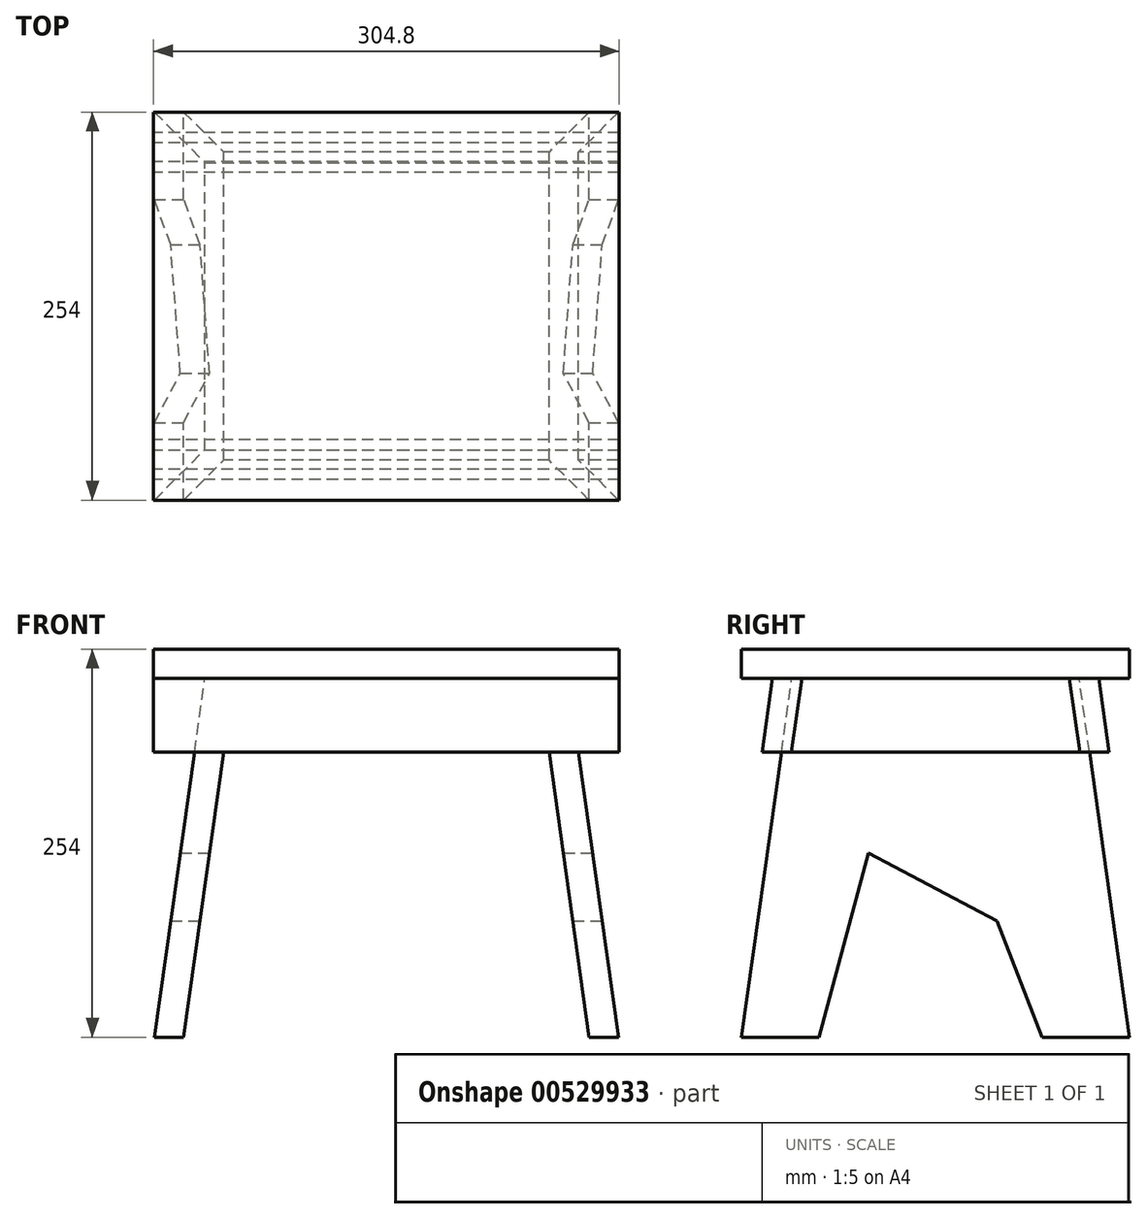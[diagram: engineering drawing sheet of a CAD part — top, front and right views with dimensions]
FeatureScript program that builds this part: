
annotation { "Feature Type Name" : "Feature", "Feature Type Description" : "" }
export const myFeature = defineFeature(function(context is Context, id is Id, definition is map)
    precondition{}
    {
        {
            var Q0;
            Q0=qCreatedBy(makeId("Front.planeOp"),FACE);
            var sketch = newSketch(context, id + "F0", { "sketchPlane" : qUnion([Q0])});
            skLineSegment(sketch, "E0.bottom", {"start": v(152.4, -9.53) * mm, "end": v(-152.4, -9.53) * mm, "construction": true});
            skLineSegment(sketch, "E0.top", {"start": v(152.4, 9.53) * mm, "end": v(-152.4, 9.52) * mm});
            skLineSegment(sketch, "E0.left", {"start": v(152.4, -9.53) * mm, "end": v(152.4, 9.52) * mm});
            skLineSegment(sketch, "E0.right", {"start": v(-152.4, -9.53) * mm, "end": v(-152.4, 9.52) * mm});
            skPoint(sketch, "E0.middle", {"position": v(0, 0) * mm});
            skLineSegment(sketch, "E1.bottom", {"start": v(-152.4, -9.53) * mm, "end": v(151.94, -9.52) * mm});
            skLineSegment(sketch, "E1.top", {"start": v(-152.4, -244.47) * mm, "end": v(151.94, -244.47) * mm, "construction": true});
            skLineSegment(sketch, "E1.left", {"start": v(-152.4, -9.53) * mm, "end": v(-152.4, -244.47) * mm, "construction": true});
            skLineSegment(sketch, "E1.right", {"start": v(151.94, -9.52) * mm, "end": v(151.94, -244.47) * mm, "construction": true});
            skLineSegment(sketch, "E2", {"start": v(118.92, -9.52) * mm, "end": v(151.94, -244.47) * mm});
            skLineSegment(sketch, "E3", {"start": v(99.68, -9.53) * mm, "end": v(132.7, -244.47) * mm});
            skLineSegment(sketch, "E4", {"start": v(99.68, -9.52) * mm, "end": v(118.92, -9.52) * mm});
            skLineSegment(sketch, "E5.MirrorCS", {"start": v(-99.68, -9.53) * mm, "end": v(-118.92, -9.53) * mm});
            skLineSegment(sketch, "E6.MirrorCS", {"start": v(-118.92, -9.53) * mm, "end": v(-151.94, -244.47) * mm});
            skLineSegment(sketch, "E7.MirrorCS", {"start": v(-99.68, -9.52) * mm, "end": v(-132.7, -244.47) * mm});
            skLineSegment(sketch, "E8.MirrorCS", {"start": v(-151.94, -9.52) * mm, "end": v(-151.94, -244.47) * mm, "construction": true});
            skLineSegment(sketch, "E9", {"start": v(0, 0) * mm, "end": v(0, -244.47) * mm, "construction": true});
            skPoint(sketch, "E9.endSnap0", {"position": v(0, -9.53) * mm});
            skLineSegment(sketch, "E10.bottom", {"start": v(-151.94, -9.53) * mm, "end": v(151.94, -9.53) * mm});
            skLineSegment(sketch, "E10.top", {"start": v(-151.94, -57.79) * mm, "end": v(151.94, -57.78) * mm});
            skLineSegment(sketch, "E10.left", {"start": v(-151.94, -9.52) * mm, "end": v(-151.94, -57.78) * mm});
            skLineSegment(sketch, "E10.right", {"start": v(151.94, -9.52) * mm, "end": v(151.94, -57.78) * mm});
            skLineSegment(sketch, "E11", {"start": v(141.11, -9.52) * mm, "end": v(134.33, -57.79) * mm});
            skLineSegment(sketch, "E12.MirrorCS", {"start": v(-141.11, -9.53) * mm, "end": v(-134.33, -57.79) * mm});
            skLineSegment(sketch, "E13", {"start": v(-135.36, -50.47) * mm, "end": v(-134.33, -57.79) * mm});
            skLineSegment(sketch, "E14", {"start": v(-152.4, 9.52) * mm, "end": v(152.4, 9.53) * mm});
            skLineSegment(sketch, "E15", {"start": v(152.4, -9.52) * mm, "end": v(-151.94, -9.52) * mm});
            skLineSegment(sketch, "E16", {"start": v(-132.7, -244.47) * mm, "end": v(-151.94, -244.47) * mm});
            skLineSegment(sketch, "E17", {"start": v(-132.7, -244.47) * mm, "end": v(-99.68, -9.53) * mm});
            skLineSegment(sketch, "E18", {"start": v(151.94, -244.47) * mm, "end": v(118.92, -9.53) * mm});
            skLineSegment(sketch, "E19", {"start": v(118.92, -9.52) * mm, "end": v(99.68, -9.52) * mm});
            skLineSegment(sketch, "E20", {"start": v(132.7, -244.47) * mm, "end": v(151.94, -244.47) * mm});
            skSolve(sketch);
        }
        {
            var Q0;
            {var subQ7=sQuery(id+"F0.wireOp",EDGE,"E0.left");Q0=makeQuery(id+"F0.imprint","IMPRINT",FACE,{"disambiguationData":[TD([[makeQuery(id+"F0.imprint","IMPRINT",EDGE,{"derivedFrom":subQ7}),1.0]])]});}
            extrude(context, id + "F1", {"entities" : qUnion([Q0]), "endBound" : BoundingType.SYMMETRIC, "depth" : 254 * mm, "offsetDistance" : 25.4 * mm});
        }
        {
            var Q0;
            {var subQ0=sQuery(id+"F0.wireOp",EDGE,"E6.MirrorCS");var subQ1=sQuery(id+"F0.wireOp",EDGE,"E10.top");var subQ2=makeQuery(id+"F0.imprint","INTERSECT",VERTEX,{"derivedFrom":[subQ1,subQ0]});Q0=makeQuery(id+"F0.imprint","IMPRINT",FACE,{"disambiguationData":[TD([[makeQuery(id+"F0.imprint","IMPRINT",EDGE,{"disambiguationData":[TD([[subQ2,-1.0]])],"derivedFrom":subQ1}),1.0]])]});}
            var Q1;
            {var subQ5=sQuery(id+"F0.wireOp",EDGE,"E16");Q1=makeQuery(id+"F0.imprint","IMPRINT",FACE,{"disambiguationData":[TD([[makeQuery(id+"F0.imprint","IMPRINT",EDGE,{"derivedFrom":subQ5}),-1.0]])]});}
            var Q2;
            {var subQ5=sQuery(id+"F0.wireOp",EDGE,"E19");Q2=makeQuery(id+"F0.imprint","IMPRINT",FACE,{"disambiguationData":[TD([[makeQuery(id+"F0.imprint","IMPRINT",EDGE,{"derivedFrom":subQ5}),1.0]])]});}
            var Q3;
            {var subQ5=sQuery(id+"F0.wireOp",EDGE,"E20");Q3=makeQuery(id+"F0.imprint","IMPRINT",FACE,{"disambiguationData":[TD([[makeQuery(id+"F0.imprint","IMPRINT",EDGE,{"derivedFrom":subQ5}),1.0]])]});}
            var Q4;
            Q4 = qSketchRegion(id + "F3", true);
            var Q5;
            Q5=makeQuery(id+"F1.opExtrude","CAP_VERTEX",VERTEX,{"disambiguationData":[OSD([sQuery(id+"F0.wireOp",EDGE,"E0.left"),sQuery(id+"F0.wireOp",EDGE,"E15")])],"isStart":false});
            var Q6;
            Q6=makeQuery(id+"F1.opExtrude","CAP_VERTEX",VERTEX,{"disambiguationData":[OSD([sQuery(id+"F0.wireOp",EDGE,"E0.left"),sQuery(id+"F0.wireOp",EDGE,"E15")])],"isStart":true});
            extrude(context, id + "F2", {"entities" : qUnion([Q0, Q1, Q2, Q3, Q4]), "endBound" : BoundingType.UP_TO_VERTEX, "depth" : 25.4 * mm, "endBoundEntityVertex" : qUnion([Q5]), "offsetDistance" : 25.4 * mm, "hasSecondDirection" : true, "secondDirectionBound" : SecondDirectionBoundingType.UP_TO_VERTEX, "secondDirectionOppositeDirection" : true, "secondDirectionDepth" : 25.4 * mm, "secondDirectionBoundEntityVertex" : qUnion([Q6])});
        }
        {
            var Q0;
            Q0=qCreatedBy(makeId("Right.planeOp"),FACE);
            var sketch = newSketch(context, id + "F3", { "sketchPlane" : qUnion([Q0])});
            skLineSegment(sketch, "E21.0.0", {"start": v(127, -9.52) * mm, "end": v(-127, -9.52) * mm});
            skLineSegment(sketch, "E21.0.1", {"start": v(-127, -9.52) * mm, "end": v(-127, -244.47) * mm});
            skLineSegment(sketch, "E21.0.2", {"start": v(-127, -244.47) * mm, "end": v(127, -244.47) * mm});
            skLineSegment(sketch, "E21.0.3", {"start": v(127, -244.47) * mm, "end": v(127, -9.52) * mm});
            skLineSegment(sketch, "E22", {"start": v(-127, -244.47) * mm, "end": v(-93.98, -9.52) * mm});
            skLineSegment(sketch, "E23.MirrorCS", {"start": v(127, -244.47) * mm, "end": v(93.98, -9.52) * mm});
            skLineSegment(sketch, "E24", {"start": v(-76.2, -244.47) * mm, "end": v(-44, -123.82) * mm});
            skLineSegment(sketch, "E25", {"start": v(-44, -123.82) * mm, "end": v(40.23, -168.27) * mm});
            skLineSegment(sketch, "E26", {"start": v(40.23, -168.27) * mm, "end": v(69.85, -244.47) * mm});
            skSolve(sketch);
        }
        {
            var Q0;
            {var subQ0=sQuery(id+"F3.wireOp",EDGE,"E24");Q0=makeQuery(id+"F3.imprint","IMPRINT",FACE,{"disambiguationData":[TD([[makeQuery(id+"F3.imprint","IMPRINT",EDGE,{"derivedFrom":subQ0}),-1.0]])]});}
            var Q1;
            {var subQ0=sQuery(id+"F3.wireOp",EDGE,"E21.0.3");Q1=makeQuery(id+"F3.imprint","IMPRINT",FACE,{"disambiguationData":[TD([[makeQuery(id+"F3.imprint","IMPRINT",EDGE,{"derivedFrom":subQ0}),1.0]])]});}
            var Q2;
            {var subQ0=sQuery(id+"F3.wireOp",EDGE,"E21.0.1");Q2=makeQuery(id+"F3.imprint","IMPRINT",FACE,{"disambiguationData":[TD([[makeQuery(id+"F3.imprint","IMPRINT",EDGE,{"derivedFrom":subQ0}),1.0]])]});}
            extrude(context, id + "F4", {"entities" : qUnion([Q0, Q1, Q2]), "operationType" : NewBodyOperationType.REMOVE, "endBound" : BoundingType.THROUGH_ALL, "oppositeDirection" : true, "depth" : 25.4 * mm, "offsetDistance" : 25.4 * mm, "hasSecondDirection" : true, "secondDirectionBound" : SecondDirectionBoundingType.THROUGH_ALL, "secondDirectionOppositeDirection" : false, "secondDirectionDepth" : 25.4 * mm});
        }
        {
            var Q0;
            Q0=qCreatedBy(makeId("Right.planeOp"),FACE);
            var sketch = newSketch(context, id + "F5", { "sketchPlane" : qUnion([Q0])});
            skLineSegment(sketch, "E27.0", {"start": v(-106.8, -9.53) * mm, "end": v(106.8, -9.53) * mm});
            skLineSegment(sketch, "E28.0", {"start": v(-93.98, -9.53) * mm, "end": v(-127, -244.47) * mm});
            skLineSegment(sketch, "E29.0", {"start": v(93.98, -9.52) * mm, "end": v(127, -244.47) * mm});
            skLineSegment(sketch, "E30", {"start": v(-106.8, -9.52) * mm, "end": v(-113.59, -57.79) * mm});
            skLineSegment(sketch, "E31", {"start": v(-113.59, -57.79) * mm, "end": v(-94.35, -57.79) * mm});
            skLineSegment(sketch, "E32", {"start": v(-94.35, -57.79) * mm, "end": v(-87.57, -9.52) * mm});
            skLineSegment(sketch, "E33", {"start": v(-87.57, -9.53) * mm, "end": v(-106.8, -9.53) * mm});
            skLineSegment(sketch, "E34", {"start": v(-94.35, -57.79) * mm, "end": v(0, -57.79) * mm});
            skLineSegment(sketch, "E35.MirrorCS", {"start": v(94.35, -57.79) * mm, "end": v(87.57, -9.52) * mm});
            skLineSegment(sketch, "E36.MirrorCS", {"start": v(94.35, -57.79) * mm, "end": v(0, -57.79) * mm});
            skLineSegment(sketch, "E37.MirrorCS", {"start": v(106.8, -9.52) * mm, "end": v(113.59, -57.79) * mm});
            skLineSegment(sketch, "E38", {"start": v(94.35, -57.79) * mm, "end": v(113.59, -57.79) * mm});
            skLineSegment(sketch, "E39", {"start": v(87.57, -9.53) * mm, "end": v(106.8, -9.53) * mm});
            skSolve(sketch);
        }
        {
            var Q0;
            {var subQ5=sQuery(id+"F5.wireOp",EDGE,"E30");Q0=makeQuery(id+"F5.imprint","IMPRINT",FACE,{"disambiguationData":[TD([[makeQuery(id+"F5.imprint","IMPRINT",EDGE,{"derivedFrom":subQ5}),1.0]])]});}
            var Q1;
            {var subQ5=sQuery(id+"F5.wireOp",EDGE,"E32");Q1=makeQuery(id+"F5.imprint","IMPRINT",FACE,{"disambiguationData":[TD([[makeQuery(id+"F5.imprint","IMPRINT",EDGE,{"derivedFrom":subQ5}),1.0]])]});}
            var Q2;
            {var subQ5=sQuery(id+"F5.wireOp",EDGE,"E37.MirrorCS");Q2=makeQuery(id+"F5.imprint","IMPRINT",FACE,{"disambiguationData":[TD([[makeQuery(id+"F5.imprint","IMPRINT",EDGE,{"derivedFrom":subQ5}),-1.0]])]});}
            var Q3;
            {var subQ5=sQuery(id+"F5.wireOp",EDGE,"E35.MirrorCS");Q3=makeQuery(id+"F5.imprint","IMPRINT",FACE,{"disambiguationData":[TD([[makeQuery(id+"F5.imprint","IMPRINT",EDGE,{"derivedFrom":subQ5}),-1.0]])]});}
            var Q4;
            Q4=makeQuery(id+"F1.opExtrude","SWEPT_FACE",FACE,{"disambiguationData":[OSD([sQuery(id+"F0.wireOp",EDGE,"E0.left")])]});
            var Q5;
            Q5=makeQuery(id+"F1.opExtrude","SWEPT_FACE",FACE,{"disambiguationData":[OSD([sQuery(id+"F0.wireOp",EDGE,"E0.right")])]});
            extrude(context, id + "F6", {"entities" : qUnion([Q0, Q1, Q2, Q3]), "endBound" : BoundingType.UP_TO_SURFACE, "depth" : 25.4 * mm, "endBoundEntityFace" : qUnion([Q4]), "offsetDistance" : 25.4 * mm, "hasSecondDirection" : true, "secondDirectionBound" : SecondDirectionBoundingType.UP_TO_SURFACE, "secondDirectionOppositeDirection" : true, "secondDirectionDepth" : 25.4 * mm, "secondDirectionBoundEntityFace" : qUnion([Q5])});
        }
    });
